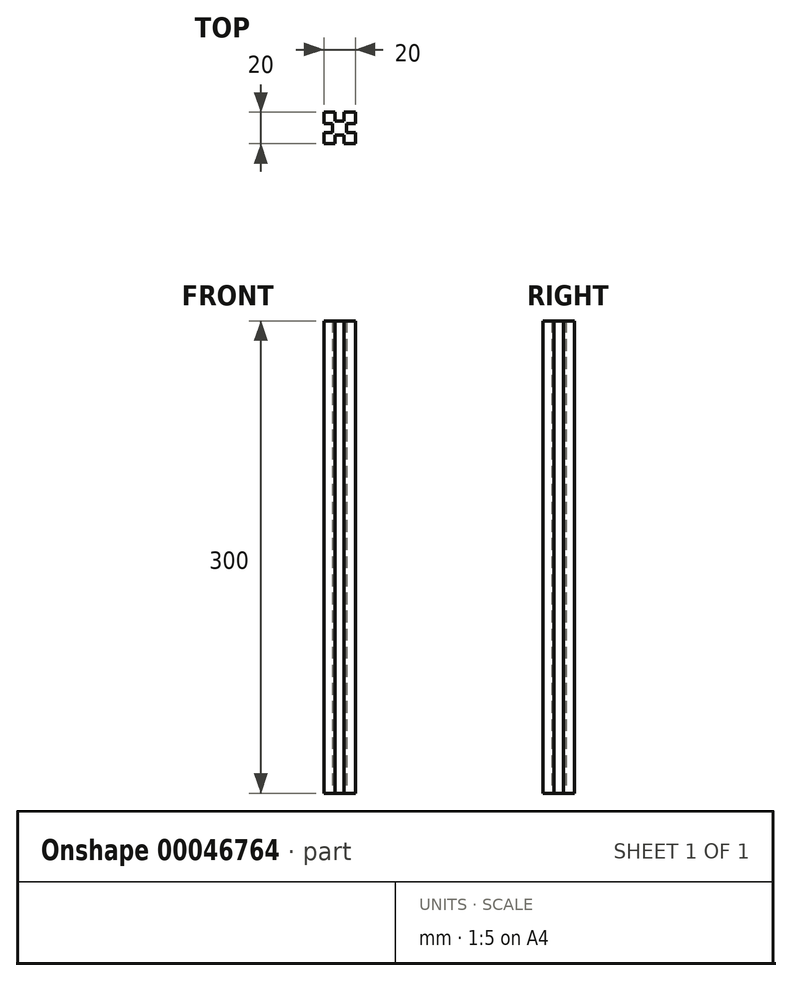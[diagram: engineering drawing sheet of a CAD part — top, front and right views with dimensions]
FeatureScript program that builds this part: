
annotation { "Feature Type Name" : "Feature", "Feature Type Description" : "" }
export const myFeature = defineFeature(function(context is Context, id is Id, definition is map)
    precondition{}
    {
        {
            var Q0;
            Q0=qCreatedBy(makeId("Top.planeOp"),FACE);
            var sketch = newSketch(context, id + "F0", { "sketchPlane" : qUnion([Q0])});
            skLineSegment(sketch, "E0.bottom", {"start": v(0, 0) * mm, "end": v(20, 0) * mm});
            skLineSegment(sketch, "E0.top", {"start": v(0, 20) * mm, "end": v(20, 20) * mm});
            skLineSegment(sketch, "E0.left", {"start": v(0, 0) * mm, "end": v(0, 20) * mm});
            skLineSegment(sketch, "E0.right", {"start": v(20, 0) * mm, "end": v(20, 20) * mm});
            skLineSegment(sketch, "E1.bottom", {"start": v(7, 20) * mm, "end": v(13, 20) * mm});
            skLineSegment(sketch, "E1.top", {"start": v(7, 14.5) * mm, "end": v(13, 14.5) * mm});
            skLineSegment(sketch, "E1.left", {"start": v(7, 20) * mm, "end": v(7, 14.5) * mm});
            skLineSegment(sketch, "E1.right", {"start": v(13, 20) * mm, "end": v(13, 14.5) * mm});
            skLineSegment(sketch, "E2.bottom", {"start": v(20, 13) * mm, "end": v(14.5, 13) * mm});
            skLineSegment(sketch, "E2.top", {"start": v(20, 7) * mm, "end": v(14.5, 7) * mm});
            skLineSegment(sketch, "E2.left", {"start": v(20, 13) * mm, "end": v(20, 7) * mm});
            skLineSegment(sketch, "E2.right", {"start": v(14.5, 13) * mm, "end": v(14.5, 7) * mm});
            skLineSegment(sketch, "E3.bottom", {"start": v(13, 0) * mm, "end": v(7, 0) * mm});
            skLineSegment(sketch, "E3.top", {"start": v(13, 5.5) * mm, "end": v(7, 5.5) * mm});
            skLineSegment(sketch, "E3.left", {"start": v(13, 0) * mm, "end": v(13, 5.5) * mm});
            skLineSegment(sketch, "E3.right", {"start": v(7, 0) * mm, "end": v(7, 5.5) * mm});
            skLineSegment(sketch, "E4.bottom", {"start": v(0, 7) * mm, "end": v(5.5, 7) * mm});
            skLineSegment(sketch, "E4.top", {"start": v(0, 13) * mm, "end": v(5.5, 13) * mm});
            skLineSegment(sketch, "E4.left", {"start": v(0, 7) * mm, "end": v(0, 13) * mm});
            skLineSegment(sketch, "E4.right", {"start": v(5.5, 7) * mm, "end": v(5.5, 13) * mm});
            skSolve(sketch);
        }
        {
            var Q0;
            Q0=makeQuery(id+"F0.imprint","IMPRINT",FACE,{"disambiguationData":[TD([[makeQuery(id+"F0.imprint","IMPRINT",EDGE,{"derivedFrom":sQuery(id+"F0.wireOp",EDGE,"E1.top")}),-1.0]])]});
            extrude(context, id + "F1", {"entities" : qUnion([Q0]), "depth" : 300 * mm});
        }
    });
